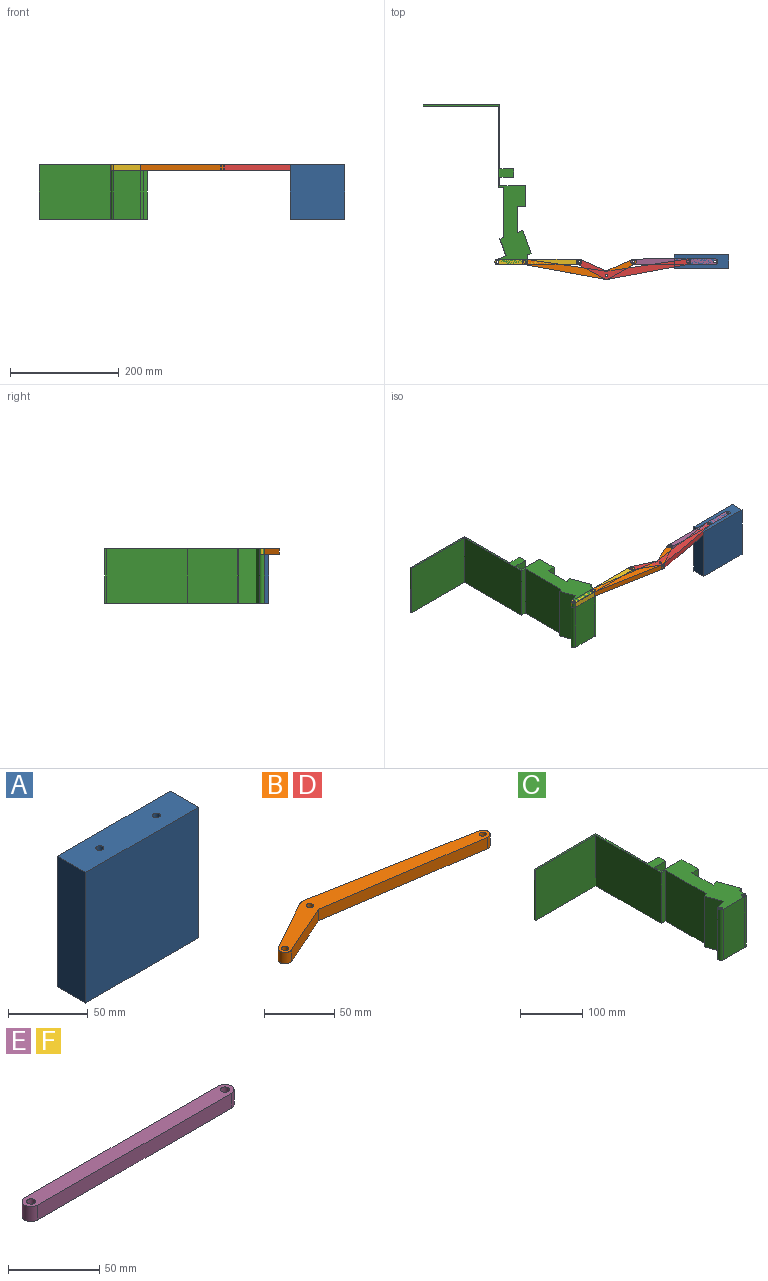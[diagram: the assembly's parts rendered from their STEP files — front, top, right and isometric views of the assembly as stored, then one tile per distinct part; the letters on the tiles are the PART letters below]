
ASSEMBLY  parts=6 mates=7
PART A: 8 faces, bbox 100x25x100 mm
  f0: plane 100x100mm, normal (0,1,0), area 10000mm2, adj f1,f5,f6,f7
  f1: plane 100x25mm, normal (-1,0,0), area 2500mm2, adj f0,f2,f6,f7
  f2: plane 100x100mm, normal (0,-1,0), area 10000mm2, adj f1,f5,f6,f7
  f3: cylinder r=2.5mm len=100mm, axis (0,0,-1), area 1570.8mm2, adj f6,f7
  f4: cylinder r=2.5mm len=100mm, axis (0,0,-1), area 1570.8mm2, adj f6,f7
  f5: plane 100x25mm, normal (1,0,0), area 2500mm2, adj f0,f2,f6,f7
  f6: plane 100x25mm, normal (0,0,1), area 2460.7mm2, adj f0,f1,f2,f3,f4,f5
  f7: plane 100x25mm, normal (0,0,-1), area 2460.7mm2, adj f0,f1,f2,f3,f4,f5
PART B: 12 faces, bbox 210x37.5x10 mm
  f0: plane 49.02x21.83mm, normal (0.41,-0.91,0), area 536.6mm2, adj f1,f9,f10,f11
  f1: plane 148.21x22.2mm, normal (-0.15,-0.99,0), area 1498.6mm2, adj f0,f2,f10,f11
  f2: cylinder r=5mm len=10mm, axis (0,0,-1), area 155.4mm2, adj f1,f3,f10,f11
  f3: plane 149.55x27.46mm, normal (0.18,0.98,0), area 1520.5mm2, adj f2,f4,f10,f11
  f4: cylinder r=7.5mm len=10mm, axis (0,0,-1), area 51.7mm2, adj f3,f5,f10,f11
  f5: plane 48.78x27.18mm, normal (-0.49,0.87,0), area 558.5mm2, adj f4,f9,f10,f11
  f6: cylinder r=2.5mm len=10mm, axis (0,0,-1), area 157.1mm2, adj f10,f11
  f7: cylinder r=2.5mm len=10mm, axis (0,0,-1), area 157.1mm2, adj f10,f11
  f8: cylinder r=2.5mm len=10mm, axis (0,0,-1), area 157.1mm2, adj f10,f11
  f9: cylinder r=5mm len=10mm, axis (0,0,-1), area 152.6mm2, adj f0,f5,f10,f11
  f10: plane 210x37.5mm, normal (0,0,1), area 2619.8mm2, adj f0,f1,f2,f3,f4,f5,f6,f7
  f11: plane 210x37.5mm, normal (0,0,-1), area 2619.8mm2, adj f0,f1,f2,f3,f4,f5,f6,f7
PART C: 29 faces, bbox 198.6x294.2x100 mm
  f0: plane 100x92.46mm, normal (-1,0,0), area 9246.3mm2, adj f1,f25,f27,f28
  f1: plane 100x7.05mm, normal (-0.34,0.94,0), area 750.2mm2, adj f0,f2,f27,f28
  f2: plane 100x31.4mm, normal (-0.94,-0.34,0), area 3341mm2, adj f1,f3,f27,f28
  f3: plane 100x16.21mm, normal (-0.34,0.94,0), area 1724.8mm2, adj f2,f4,f27,f28
  f4: cylinder r=5mm len=100mm, axis (0,0,-1), area 1509.9mm2, adj f3,f5,f27,f28
  f5: plane 100x48.9mm, normal (0,-1,0), area 4890.1mm2, adj f4,f6,f27,f28
  f6: cylinder r=5mm len=100mm, axis (0,0,-1), area 1017mm2, adj f5,f7,f27,f28
  f7: plane 100x11.61mm, normal (1,0,0), area 1160.9mm2, adj f6,f8,f27,f28
  f8: plane 100x6.99mm, normal (0.34,-0.94,0), area 743.5mm2, adj f7,f9,f27,f28
  f9: plane 100x42.29mm, normal (0.94,0.34,0), area 4500mm2, adj f8,f10,f27,f28
  f10: plane 100x10.34mm, normal (-0.34,0.94,0), area 1100mm2, adj f9,f11,f27,f28
  f11: plane 100x48.6mm, normal (1,0,0), area 4860mm2, adj f10,f12,f27,f28
  f12: plane 100x15mm, normal (0,-1,0), area 1500mm2, adj f11,f13,f27,f28
  f13: plane 100x37.8mm, normal (1,0,0), area 3780mm2, adj f12,f14,f27,f28
  f14: plane 100x46.9mm, normal (0,1,0), area 4690mm2, adj f13,f15,f27,f28
  f15: plane 100x15mm, normal (1,0,0), area 1500mm2, adj f14,f16,f27,f28
  f16: plane 100x25.2mm, normal (0,-1,0), area 2520mm2, adj f15,f17,f27,f28
  f17: plane 100x15.7mm, normal (1,0,0), area 1570mm2, adj f16,f18,f27,f28
  f18: plane 100x25.2mm, normal (0,1,0), area 2520mm2, adj f17,f19,f27,f28
  f19: plane 118.21x100mm, normal (1,0,0), area 11820.8mm2, adj f18,f20,f27,f28
  f20: plane 140.93x100mm, normal (0,1,0), area 14093mm2, adj f19,f21,f27,f28
  f21: plane 100x3mm, normal (-1,0,0), area 300mm2, adj f20,f22,f27,f28
  f22: plane 137.93x100mm, normal (0,-1,0), area 13793mm2, adj f21,f23,f27,f28
  f23: plane 148.91x100mm, normal (-1,0,0), area 14890.8mm2, adj f22,f25,f27,f28
  f24: cylinder r=2.5mm len=100mm, axis (0,0,-1), area 1570.8mm2, adj f27,f28
  f25: plane 100x10mm, normal (0,-1,0), area 1000mm2, adj f0,f23,f27,f28
  f26: cylinder r=2.5mm len=100mm, axis (0,0,-1), area 1570.8mm2, adj f27,f28
  f27: plane 294.19x198.56mm, normal (0,0,1), area 6781.4mm2, adj f0,f1,f2,f3,f4,f5,f6,f7
  f28: plane 294.19x198.56mm, normal (0,0,-1), area 6781.4mm2, adj f0,f1,f2,f3,f4,f5,f6,f7
PART D: same geometry as B
PART E: 8 faces, bbox 160x10x10 mm
  f0: cylinder r=5mm len=10mm, axis (0,0,-1), area 157.1mm2, adj f1,f5,f6,f7
  f1: plane 150x10mm, normal (0,-1,0), area 1500mm2, adj f0,f2,f6,f7
  f2: cylinder r=5mm len=10mm, axis (0,0,-1), area 157.1mm2, adj f1,f5,f6,f7
  f3: cylinder r=2.5mm len=10mm, axis (0,0,-1), area 157.1mm2, adj f6,f7
  f4: cylinder r=2.5mm len=10mm, axis (0,0,-1), area 157.1mm2, adj f6,f7
  f5: plane 150x10mm, normal (0,1,0), area 1500mm2, adj f0,f2,f6,f7
  f6: plane 160x10mm, normal (0,0,1), area 1539.3mm2, adj f0,f1,f2,f3,f4,f5
  f7: plane 160x10mm, normal (0,0,-1), area 1539.3mm2, adj f0,f1,f2,f3,f4,f5
PART F: same geometry as E
PLACE A rot(axis=(0,0,1),0.2deg) t=(241.83,-127.5,0)mm
PLACE B rot(axis=(0,0,-1),179.9deg) t=(9.38,-392.69,90)mm
PLACE C at identity fixed
PLACE D rot(axis=(1,0,0),180deg) t=(289.17,-392.26,100)mm
PLACE E rot(axis=(0,0,1),0.1deg) t=(267.63,67.55,90)mm
PLACE F rot(axis=(0,0,1),0.1deg) t=(17.84,67.17,90)mm
MATE revolute F.f0 <-> C.f4  axis (0,0,1) through (-51.11,-140.28,100)mm
MATE revolute B.f2 <-> C.f6  axis (0,0,1) through (-1.11,-140.28,100)mm
MATE revolute F.f2 <-> D.f7  axis (0,0,1) through (98.89,-140.13,100)mm
MATE revolute D.f4 <-> B.f4  axis (0,0,1) through (148.93,-165.06,100)mm
MATE revolute D.f2 <-> A.f3  axis (0,0,1) through (298.89,-139.83,100)mm
MATE revolute E.f2 <-> A.f4  axis (0,0,1) through (348.89,-139.68,100)mm
MATE revolute E.f0 <-> B.f7  axis (0,0,1) through (198.89,-139.98,100)mm
